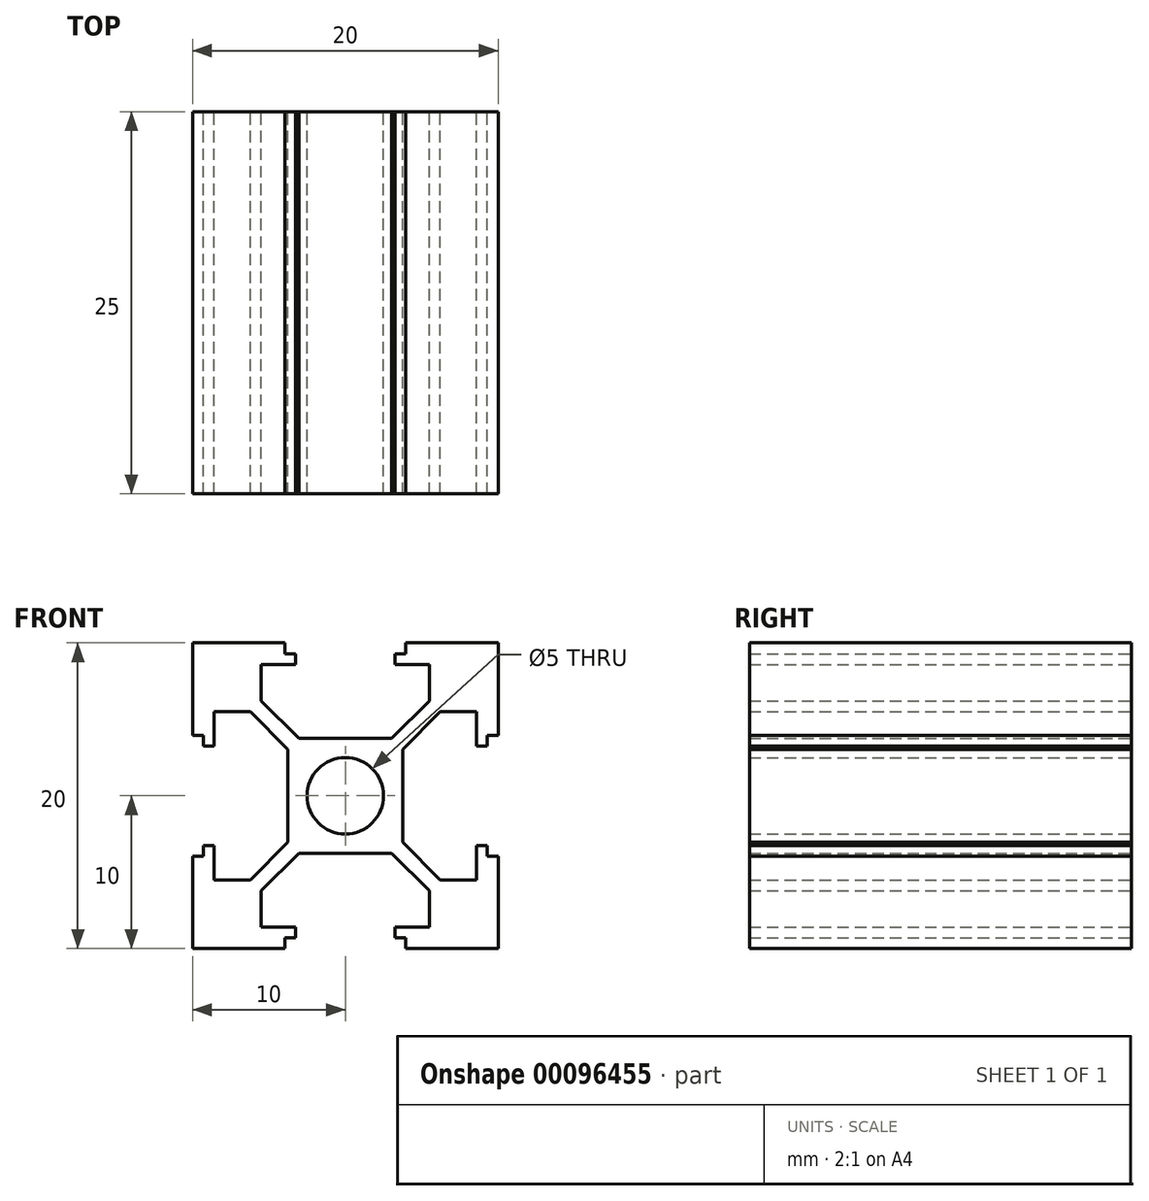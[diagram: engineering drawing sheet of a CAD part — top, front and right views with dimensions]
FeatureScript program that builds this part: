
annotation { "Feature Type Name" : "Feature", "Feature Type Description" : "" }
export const myFeature = defineFeature(function(context is Context, id is Id, definition is map)
    precondition{}
    {
        {
            var Q0;
            Q0=qCreatedBy(makeId("Front.planeOp"),FACE);
            var sketch = newSketch(context, id + "F0", { "sketchPlane" : qUnion([Q0])});
            skLineSegment(sketch, "E0.bottom", {"start": v(0, 0) * mm, "end": v(10, 0) * mm, "construction": true});
            skLineSegment(sketch, "E0.top", {"start": v(0, 10) * mm, "end": v(10, 10) * mm, "construction": true});
            skLineSegment(sketch, "E0.left", {"start": v(0, 0) * mm, "end": v(0, 10) * mm, "construction": true});
            skLineSegment(sketch, "E0.right", {"start": v(10, 0) * mm, "end": v(10, 10) * mm, "construction": true});
            skLineSegment(sketch, "E1", {"start": v(0, 0) * mm, "end": v(10, 10) * mm, "construction": true});
            skLineSegment(sketch, "E2", {"start": v(10, 10) * mm, "end": v(10, 3.95) * mm});
            skLineSegment(sketch, "E3", {"start": v(10, 3.95) * mm, "end": v(9.3, 3.95) * mm});
            skLineSegment(sketch, "E4", {"start": v(9.3, 3.95) * mm, "end": v(9.3, 3.25) * mm});
            skLineSegment(sketch, "E5", {"start": v(9.3, 3.25) * mm, "end": v(8.6, 3.25) * mm});
            skLineSegment(sketch, "E6", {"start": v(8.6, 3.25) * mm, "end": v(8.6, 5.5) * mm});
            skLineSegment(sketch, "E7", {"start": v(8.6, 5.5) * mm, "end": v(6.2, 5.5) * mm});
            skLineSegment(sketch, "E8", {"start": v(6.2, 5.5) * mm, "end": v(3.75, 3.04) * mm});
            skLineSegment(sketch, "E9", {"start": v(3.75, 3.04) * mm, "end": v(3.75, 0) * mm});
            skLineSegment(sketch, "E10.MirrorCS", {"start": v(3.25, 9.3) * mm, "end": v(3.25, 8.6) * mm});
            skLineSegment(sketch, "E11.MirrorCS", {"start": v(3.95, 10) * mm, "end": v(3.95, 9.3) * mm});
            skLineSegment(sketch, "E12.MirrorCS", {"start": v(3.95, 9.3) * mm, "end": v(3.25, 9.3) * mm});
            skLineSegment(sketch, "E13.MirrorCS", {"start": v(10, 10) * mm, "end": v(3.95, 10) * mm});
            skLineSegment(sketch, "E14.MirrorCS", {"start": v(3.25, 8.6) * mm, "end": v(5.5, 8.6) * mm});
            skLineSegment(sketch, "E15.MirrorCS", {"start": v(5.5, 8.6) * mm, "end": v(5.5, 6.2) * mm});
            skLineSegment(sketch, "E16.MirrorCS", {"start": v(3.04, 3.75) * mm, "end": v(0, 3.75) * mm});
            skLineSegment(sketch, "E17.MirrorCS", {"start": v(5.5, 6.2) * mm, "end": v(3.04, 3.75) * mm});
            skLineSegment(sketch, "E18.1.0", {"start": v(-8.6, 5.5) * mm, "end": v(-6.2, 5.5) * mm});
            skLineSegment(sketch, "E18.1.1", {"start": v(-8.6, 3.25) * mm, "end": v(-8.6, 5.5) * mm});
            skLineSegment(sketch, "E18.1.2", {"start": v(-10, 10) * mm, "end": v(-10, 3.95) * mm});
            skLineSegment(sketch, "E18.1.3", {"start": v(-3.75, 3.04) * mm, "end": v(-3.75, 0) * mm});
            skLineSegment(sketch, "E18.1.5", {"start": v(-10, 0) * mm, "end": v(-10, 10) * mm, "construction": true});
            skLineSegment(sketch, "E18.1.6", {"start": v(0, 0) * mm, "end": v(-10, 0) * mm, "construction": true});
            skLineSegment(sketch, "E18.1.7", {"start": v(0, 10) * mm, "end": v(-10, 10) * mm, "construction": true});
            skLineSegment(sketch, "E18.1.8", {"start": v(0, 0) * mm, "end": v(-10, 10) * mm, "construction": true});
            skLineSegment(sketch, "E18.1.9", {"start": v(-10, 10) * mm, "end": v(-3.95, 10) * mm});
            skLineSegment(sketch, "E18.1.10", {"start": v(-3.25, 8.6) * mm, "end": v(-5.5, 8.6) * mm});
            skLineSegment(sketch, "E18.1.11", {"start": v(-5.5, 8.6) * mm, "end": v(-5.5, 6.2) * mm});
            skLineSegment(sketch, "E18.1.12", {"start": v(-5.5, 6.2) * mm, "end": v(-3.04, 3.75) * mm});
            skLineSegment(sketch, "E18.1.13", {"start": v(-3.04, 3.75) * mm, "end": v(0, 3.75) * mm});
            skLineSegment(sketch, "E18.1.14", {"start": v(-6.2, 5.5) * mm, "end": v(-3.75, 3.04) * mm});
            skLineSegment(sketch, "E18.1.15", {"start": v(-9.3, 3.25) * mm, "end": v(-8.6, 3.25) * mm});
            skLineSegment(sketch, "E18.1.16", {"start": v(-10, 3.95) * mm, "end": v(-9.3, 3.95) * mm});
            skLineSegment(sketch, "E18.1.17", {"start": v(-9.3, 3.95) * mm, "end": v(-9.3, 3.25) * mm});
            skLineSegment(sketch, "E18.1.18", {"start": v(-3.95, 10) * mm, "end": v(-3.95, 9.3) * mm});
            skLineSegment(sketch, "E18.1.19", {"start": v(-3.95, 9.3) * mm, "end": v(-3.25, 9.3) * mm});
            skLineSegment(sketch, "E18.1.20", {"start": v(-3.25, 9.3) * mm, "end": v(-3.25, 8.6) * mm});
            skLineSegment(sketch, "E18.2.0", {"start": v(-5.5, -8.6) * mm, "end": v(-5.5, -6.2) * mm});
            skLineSegment(sketch, "E18.2.1", {"start": v(-3.25, -8.6) * mm, "end": v(-5.5, -8.6) * mm});
            skLineSegment(sketch, "E18.2.2", {"start": v(-10, -10) * mm, "end": v(-3.95, -10) * mm});
            skLineSegment(sketch, "E18.2.3", {"start": v(-3.04, -3.75) * mm, "end": v(0, -3.75) * mm});
            skLineSegment(sketch, "E18.2.4", {"start": v(0, 0) * mm, "end": v(-10, 0) * mm, "construction": true});
            skLineSegment(sketch, "E18.2.5", {"start": v(0, -10) * mm, "end": v(-10, -10) * mm, "construction": true});
            skLineSegment(sketch, "E18.2.6", {"start": v(0, 0) * mm, "end": v(0, -10) * mm, "construction": true});
            skLineSegment(sketch, "E18.2.7", {"start": v(-10, 0) * mm, "end": v(-10, -10) * mm, "construction": true});
            skLineSegment(sketch, "E18.2.8", {"start": v(0, 0) * mm, "end": v(-10, -10) * mm, "construction": true});
            skLineSegment(sketch, "E18.2.9", {"start": v(-10, -10) * mm, "end": v(-10, -3.95) * mm});
            skLineSegment(sketch, "E18.2.10", {"start": v(-8.6, -3.25) * mm, "end": v(-8.6, -5.5) * mm});
            skLineSegment(sketch, "E18.2.11", {"start": v(-8.6, -5.5) * mm, "end": v(-6.2, -5.5) * mm});
            skLineSegment(sketch, "E18.2.12", {"start": v(-6.2, -5.5) * mm, "end": v(-3.75, -3.04) * mm});
            skLineSegment(sketch, "E18.2.13", {"start": v(-3.75, -3.04) * mm, "end": v(-3.75, 0) * mm});
            skLineSegment(sketch, "E18.2.14", {"start": v(-5.5, -6.2) * mm, "end": v(-3.04, -3.75) * mm});
            skLineSegment(sketch, "E18.2.15", {"start": v(-3.25, -9.3) * mm, "end": v(-3.25, -8.6) * mm});
            skLineSegment(sketch, "E18.2.16", {"start": v(-3.95, -10) * mm, "end": v(-3.95, -9.3) * mm});
            skLineSegment(sketch, "E18.2.17", {"start": v(-3.95, -9.3) * mm, "end": v(-3.25, -9.3) * mm});
            skLineSegment(sketch, "E18.2.18", {"start": v(-10, -3.95) * mm, "end": v(-9.3, -3.95) * mm});
            skLineSegment(sketch, "E18.2.19", {"start": v(-9.3, -3.95) * mm, "end": v(-9.3, -3.25) * mm});
            skLineSegment(sketch, "E18.2.20", {"start": v(-9.3, -3.25) * mm, "end": v(-8.6, -3.25) * mm});
            skPoint(sketch, "E18.center", {"position": v(0, 0) * mm});
            skLineSegment(sketch, "E19.2.3.0", {"start": v(8.6, -5.5) * mm, "end": v(6.2, -5.5) * mm});
            skLineSegment(sketch, "E19.3.3.0", {"start": v(8.6, -3.25) * mm, "end": v(8.6, -5.5) * mm});
            skLineSegment(sketch, "E19.6.3.0", {"start": v(10, -10) * mm, "end": v(10, -3.95) * mm});
            skLineSegment(sketch, "E19.9.3.0", {"start": v(3.75, -3.04) * mm, "end": v(3.75, 0) * mm});
            skLineSegment(sketch, "E19.15.3.0", {"start": v(10, 0) * mm, "end": v(10, -10) * mm, "construction": true});
            skLineSegment(sketch, "E19.21.3.0", {"start": v(0, -10) * mm, "end": v(10, -10) * mm, "construction": true});
            skLineSegment(sketch, "E19.24.3.0", {"start": v(0, 0) * mm, "end": v(10, -10) * mm, "construction": true});
            skLineSegment(sketch, "E19.27.3.0", {"start": v(10, -10) * mm, "end": v(3.95, -10) * mm});
            skLineSegment(sketch, "E19.30.3.0", {"start": v(3.25, -8.6) * mm, "end": v(5.5, -8.6) * mm});
            skLineSegment(sketch, "E19.33.3.0", {"start": v(5.5, -8.6) * mm, "end": v(5.5, -6.2) * mm});
            skLineSegment(sketch, "E19.36.3.0", {"start": v(5.5, -6.2) * mm, "end": v(3.04, -3.75) * mm});
            skLineSegment(sketch, "E19.39.3.0", {"start": v(3.04, -3.75) * mm, "end": v(0, -3.75) * mm});
            skLineSegment(sketch, "E19.42.3.0", {"start": v(6.2, -5.5) * mm, "end": v(3.75, -3.04) * mm});
            skLineSegment(sketch, "E19.45.3.0", {"start": v(9.3, -3.25) * mm, "end": v(8.6, -3.25) * mm});
            skLineSegment(sketch, "E19.48.3.0", {"start": v(10, -3.95) * mm, "end": v(9.3, -3.95) * mm});
            skLineSegment(sketch, "E19.51.3.0", {"start": v(9.3, -3.95) * mm, "end": v(9.3, -3.25) * mm});
            skLineSegment(sketch, "E19.54.3.0", {"start": v(3.95, -10) * mm, "end": v(3.95, -9.3) * mm});
            skLineSegment(sketch, "E19.57.3.0", {"start": v(3.95, -9.3) * mm, "end": v(3.25, -9.3) * mm});
            skLineSegment(sketch, "E19.60.3.0", {"start": v(3.25, -9.3) * mm, "end": v(3.25, -8.6) * mm});
            skCircle(sketch, "E20", {"center": v(0, 0) * mm, "radius": 2.5 * mm});
            skSolve(sketch);
        }
        {
            var Q0;
            Q0=makeQuery(id+"F0.imprint","IMPRINT",FACE,{"disambiguationData":[TD([[makeQuery(id+"F0.imprint","IMPRINT",EDGE,{"derivedFrom":sQuery(id+"F0.wireOp",EDGE,"E2")}),-1.0]])]});
            extrude(context, id + "F1", {"entities" : qUnion([Q0]), "depth" : 25 * mm});
        }
    });
